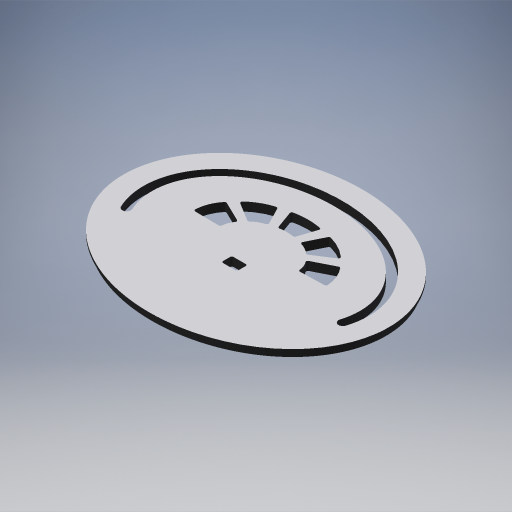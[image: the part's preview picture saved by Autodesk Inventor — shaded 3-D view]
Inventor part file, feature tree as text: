
AUTODESK INVENTOR PART (.ipt)
format: ipt  version: 2024.3 (Build 283343000, 343)  size: 647,680 bytes
history: native  units: mm
features: reference x57, sketch x10, extrude x8, projected_geometry x4, other x3, hole x2, fillet x1
ambient origin geometry x8: Origin, YZ Plane, XZ Plane, XY Plane, X Axis, Y Axis, Z Axis, Center Point
bodies: Volumenkörper1 (feature_tree)
feature tree (85):
  extrude  "Extrusion1"  Depth=240.0mm
  extrude  "Extrusion2"  Depth=10.0mm
  sketch  "Skizze3"  dims[d2=10.0mm d3=0.0mm d7=20.0mm]
  extrude  "Extrusion3"  Depth=30.0mm
  extrude  "Extrusion4"  TaperAngle=45.0deg  [1 undecoded]
  extrude  "Extrusion5"  Depth=9.919051mm
  extrude  "Extrusion6"  TaperAngle=15.0deg  [1 undecoded]
  hole  "Bohrung1"  [1 undecoded]
  extrude  "Extrusion7"  TaperAngle=0.0deg  [1 undecoded]
  fillet  "Rundung1"  [1 undecoded]
  hole  "Bohrung2"  [1 undecoded]
  extrude  "Extrusion8"  Depth=3.0mm
  sketch  "Skizze2"  dims[d0=300.0mm d1=240.0mm]
  projected_geometry  "Projizierte Kontur1"
  projected_geometry  "Projizierte Kontur2"
  sketch  "Skizze4"  dims[d8=20.0mm d9=30.0mm]
  reference  "Referenz1"
  reference  "Referenz2"
  reference  "Referenz3"
  reference  "Referenz4"
  reference  "Referenz5"
  reference  "Referenz6"
  reference  "Referenz7"
  reference  "Referenz8"
  reference  "Referenz9"
  reference  "Referenz10"
  reference  "Referenz11"
  reference  "Referenz12"
  reference  "Referenz13"
  reference  "Referenz14"
  reference  "Referenz15"
  reference  "Referenz16"
  reference  "Referenz17"
  reference  "Referenz18"
  reference  "Referenz19"
  reference  "Referenz20"
  reference  "Referenz21"
  reference  "Referenz22"
  reference  "Referenz23"
  sketch  "Skizze5"  dims[d10=30.0mm d11=45.0deg]
  reference  "Referenz24"
  reference  "Referenz25"
  reference  "Referenz26"
  reference  "Referenz27"
  reference  "Referenz28"
  reference  "Referenz29"
  reference  "Referenz30"
  reference  "Referenz31"
  reference  "Referenz32"
  reference  "Referenz33"
  reference  "Referenz34"
  reference  "Referenz35"
  sketch  "Skizze6"  dims[d12=90.0deg d13=9.919051mm]
  reference  "Referenz36"
  reference  "Referenz37"
  reference  "Referenz38"
  reference  "Referenz39"
  reference  "Referenz40"
  reference  "Referenz41"
  sketch  "Skizze7"  dims[d14=1.745329mm d15=15.0deg]
  reference  "Referenz42"
  reference  "Referenz43"
  reference  "Referenz44"
  reference  "Referenz45"
  sketch  "Skizze8"  dims[d16=0.0mm d17=0.0mm d18=75.0mm]
  reference  "Referenz46"
  reference  "Referenz47"
  reference  "Referenz48"
  reference  "Referenz49"
  reference  "Referenz50"
  reference  "Referenz51"
  reference  "Referenz52"
  reference  "Referenz53"
  reference  "Referenz54"
  reference  "Referenz55"
  reference  "Referenz56"
  reference  "Referenz57"
  sketch  "Skizze9"  dims[d19=60.0mm d20=0.0mm d21=0.0mm d22=0.0mm d23=0.0mm]
  projected_geometry  "Projizierte Kontur3"
  sketch  "Skizze10"  dims[d24=0.0mm d25=0.0mm d26=0.0mm d27=0.0mm]
  sketch  "Skizze11"  dims[d28=3.242mm d29=6.0mm d30=9.2mm d31=2.0mm d32=90.0deg d33=7.5mm d34=20.594885mm d35=1.0mm d36=1.0mm d37=1.0mm d38=1.0mm d39=1.0mm d40=1.0mm d41=10.0mm d42=0.0mm d43=2.0mm d44=5.0mm d45=5.0mm d46=6.108652mm d47=12.217305mm d48=71.86732mm d49=80.82243mm d50=3.242mm d51=6.0mm d52=4.0mm d53=2.0mm d54=90.0deg d55=7.5mm d56=20.594885mm d57=30.0deg d58=153.0mm d59=123.0mm d60=3.0mm d61=0.0mm]
  projected_geometry  "Projizierte Kontur4"
  other  "<path> - Kompass, Gehäuse\24_0497_0001.iam"
  other  "24_0497_0001.iam"
  other  "Werkstatt Modelle v10:1"
note: 6 required parameter values undecoded (feature->parameter linkage not recoverable at this tier; creation-order binding heuristic only, values carry confidence <= 0.55)
note: 1 file-system path scrubbed to <path> (originals preserved in map.json)
